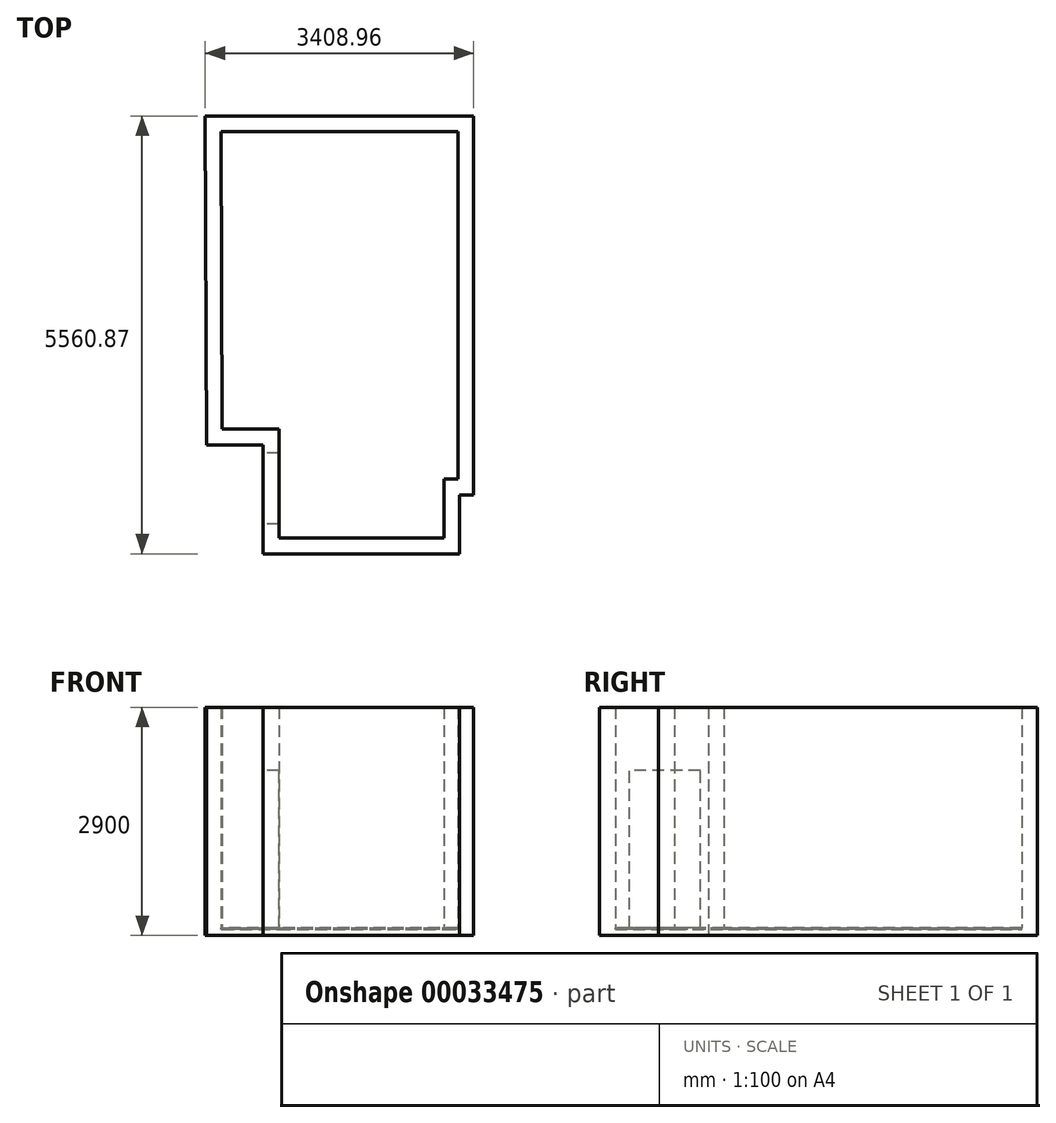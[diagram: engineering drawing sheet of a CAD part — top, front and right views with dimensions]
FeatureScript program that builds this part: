
annotation { "Feature Type Name" : "Feature", "Feature Type Description" : "" }
export const myFeature = defineFeature(function(context is Context, id is Id, definition is map)
    precondition{}
    {
        {
            var Q0;
            Q0=qCreatedBy(makeId("Top.planeOp"),FACE);
            var sketch = newSketch(context, id + "F0", { "sketchPlane" : qUnion([Q0])});
            skLineSegment(sketch, "E0", {"start": v(-1477.33, -3711.86) * mm, "end": v(-757.37, -3711.86) * mm});
            skLineSegment(sketch, "E1", {"start": v(-757.37, -3711.86) * mm, "end": v(-757.37, -5094.18) * mm});
            skLineSegment(sketch, "E2", {"start": v(-757.37, -5094.18) * mm, "end": v(1337.7, -5094.18) * mm});
            skLineSegment(sketch, "E3", {"start": v(1337.7, -5094.18) * mm, "end": v(1337.7, -4345.43) * mm});
            skLineSegment(sketch, "E4", {"start": v(1337.7, -4345.43) * mm, "end": v(1517.7, -4345.43) * mm});
            skLineSegment(sketch, "E5", {"start": v(1517.7, -4345.43) * mm, "end": v(1517.7, 67.91) * mm});
            skLineSegment(sketch, "E6", {"start": v(1517.7, 67.91) * mm, "end": v(-1491.73, 67.91) * mm});
            skLineSegment(sketch, "E7", {"start": v(-1491.73, 67.91) * mm, "end": v(-1477.33, -3711.86) * mm});
            skLineSegment(sketch, "E8.0", {"start": v(1537.1, -4544.81) * mm, "end": v(1717.08, -4544.81) * mm});
            skLineSegment(sketch, "E8.1", {"start": v(1537.1, -5293.57) * mm, "end": v(1537.1, -4544.81) * mm});
            skLineSegment(sketch, "E8.2", {"start": v(-956.76, -5293.57) * mm, "end": v(1537.1, -5293.57) * mm});
            skLineSegment(sketch, "E8.3", {"start": v(-956.76, -3911.25) * mm, "end": v(-956.76, -5293.57) * mm});
            skLineSegment(sketch, "E8.4", {"start": v(-1675.96, -3911.25) * mm, "end": v(-956.76, -3911.25) * mm});
            skLineSegment(sketch, "E8.5", {"start": v(1717.08, -4544.81) * mm, "end": v(1717.08, 267.3) * mm});
            skLineSegment(sketch, "E8.6", {"start": v(-1691.88, 267.3) * mm, "end": v(-1675.96, -3911.25) * mm});
            skLineSegment(sketch, "E8.7", {"start": v(1717.08, 267.3) * mm, "end": v(-1691.88, 267.3) * mm});
            skSolve(sketch);
        }
        {
            var Q0;
            Q0=makeQuery(id+"F0.imprint","IMPRINT",FACE,{"disambiguationData":[TD([[makeQuery(id+"F0.imprint","IMPRINT",EDGE,{"derivedFrom":sQuery(id+"F0.wireOp",EDGE,"E0")}),-1.0]])]});
            extrude(context, id + "F1", {"entities" : qUnion([Q0]), "depth" : 2800 * mm});
        }
        {
            var Q0;
            Q0=makeQuery(id+"F1.opExtrude","SWEPT_FACE",FACE,{"disambiguationData":[OSD([sQuery(id+"F0.wireOp",EDGE,"E8.3")])]});
            var sketch = newSketch(context, id + "F2", { "sketchPlane" : qUnion([Q0])});
            skLineSegment(sketch, "E9.bottom", {"start": v(4013.5, 0) * mm, "end": v(4913.5, 0) * mm});
            skLineSegment(sketch, "E9.top", {"start": v(4013.5, 2000) * mm, "end": v(4913.5, 2000) * mm});
            skLineSegment(sketch, "E9.left", {"start": v(4013.5, 0) * mm, "end": v(4013.5, 2000) * mm});
            skLineSegment(sketch, "E9.right", {"start": v(4913.5, 0) * mm, "end": v(4913.5, 2000) * mm});
            skSolve(sketch);
        }
        {
            var Q0;
            Q0=makeQuery(id+"F2.imprint","IMPRINT",FACE,{"disambiguationData":[TD([[makeQuery(id+"F2.imprint","IMPRINT",EDGE,{"derivedFrom":sQuery(id+"F2.wireOp",EDGE,"E9.bottom")}),1.0]])]});
            extrude(context, id + "F3", {"entities" : qUnion([Q0]), "operationType" : NewBodyOperationType.REMOVE, "endBound" : BoundingType.UP_TO_NEXT, "oppositeDirection" : true, "depth" : 25 * mm});
        }
        {
            var Q0;
            Q0=makeQuery(id+"F0.imprint","IMPRINT",FACE,{"disambiguationData":[TD([[makeQuery(id+"F0.imprint","IMPRINT",EDGE,{"derivedFrom":sQuery(id+"F0.wireOp",EDGE,"E0")}),-1.0]])]});
            var Q1;
            Q1=makeQuery(id+"F0.imprint","IMPRINT",FACE,{"disambiguationData":[TD([[makeQuery(id+"F0.imprint","IMPRINT",EDGE,{"derivedFrom":sQuery(id+"F0.wireOp",EDGE,"E0")}),1.0]])]});
            extrude(context, id + "F4", {"entities" : qUnion([Q0, Q1]), "operationType" : NewBodyOperationType.ADD, "oppositeDirection" : true, "depth" : 100 * mm});
        }
        {
            var Q0;
            Q0=makeQuery(id+"F0.imprint","IMPRINT",FACE,{"disambiguationData":[TD([[makeQuery(id+"F0.imprint","IMPRINT",EDGE,{"derivedFrom":sQuery(id+"F0.wireOp",EDGE,"E0")}),1.0]])]});
            extrude(context, id + "F5", {"entities" : qUnion([Q0]), "oppositeDirection" : true, "depth" : 25 * mm});
        }
    });
